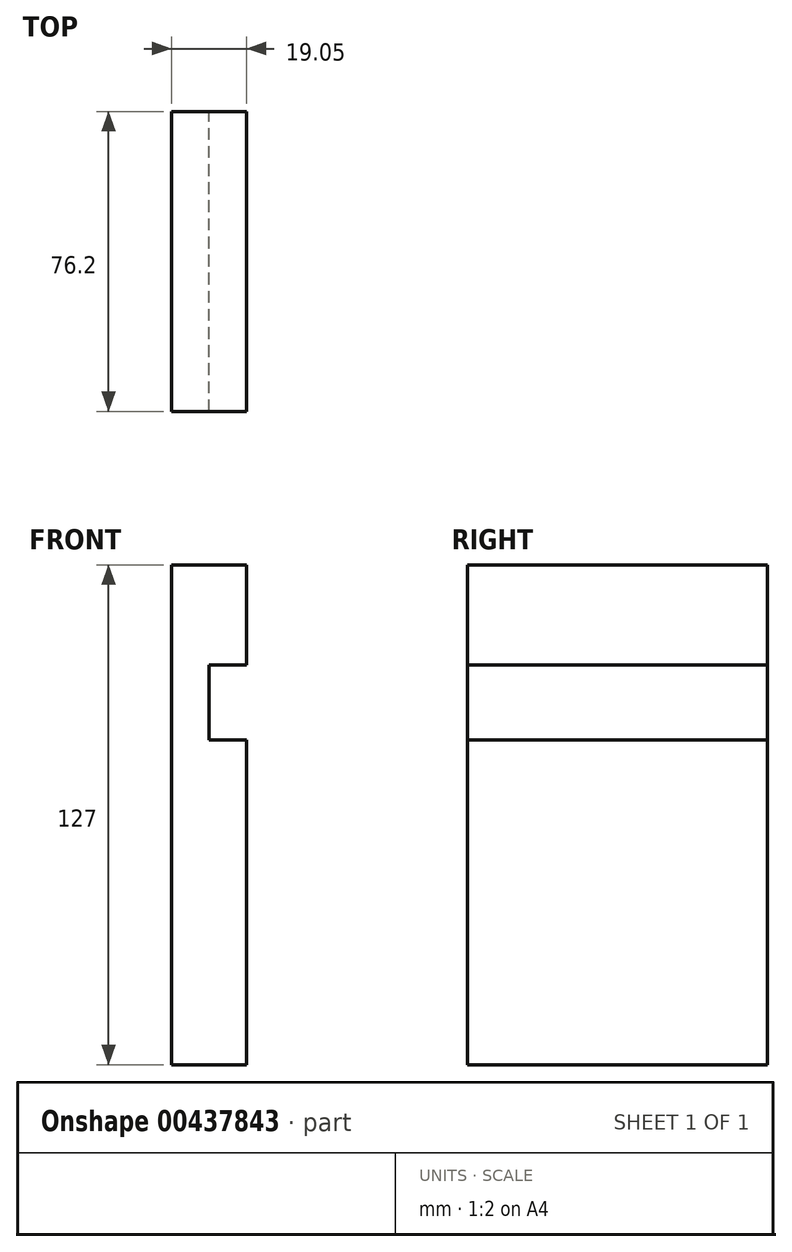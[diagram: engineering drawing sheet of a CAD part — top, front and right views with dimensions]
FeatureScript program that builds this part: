
annotation { "Feature Type Name" : "Feature", "Feature Type Description" : "" }
export const myFeature = defineFeature(function(context is Context, id is Id, definition is map)
    precondition{}
    {
        {
            var Q0;
            Q0=qCreatedBy(makeId("Front.planeOp"),FACE);
            var sketch = newSketch(context, id + "F0", { "sketchPlane" : qUnion([Q0])});
            skLineSegment(sketch, "E0", {"start": v(0, 67.4) * mm, "end": v(19.05, 67.4) * mm});
            skLineSegment(sketch, "E1", {"start": v(19.05, 67.4) * mm, "end": v(19.05, 42) * mm});
            skLineSegment(sketch, "E2", {"start": v(19.05, 42) * mm, "end": v(9.53, 42) * mm});
            skLineSegment(sketch, "E3", {"start": v(9.53, 42) * mm, "end": v(9.53, 22.96) * mm});
            skLineSegment(sketch, "E4", {"start": v(9.53, 22.96) * mm, "end": v(19.05, 22.96) * mm});
            skLineSegment(sketch, "E5", {"start": v(19.05, 22.96) * mm, "end": v(19.05, -59.6) * mm});
            skLineSegment(sketch, "E6", {"start": v(19.05, -59.6) * mm, "end": v(0, -59.6) * mm});
            skLineSegment(sketch, "E7", {"start": v(0, -59.6) * mm, "end": v(0, 67.4) * mm});
            skSolve(sketch);
        }
        {
            var Q0;
            Q0=makeQuery(id+"F0.imprint","IMPRINT",FACE,{"disambiguationData":[TD([[makeQuery(id+"F0.imprint","IMPRINT",EDGE,{"derivedFrom":sQuery(id+"F0.wireOp",EDGE,"E0")}),-1.0]])]});
            extrude(context, id + "F1", {"entities" : qUnion([Q0]), "depth" : 76.2 * mm});
        }
    });
